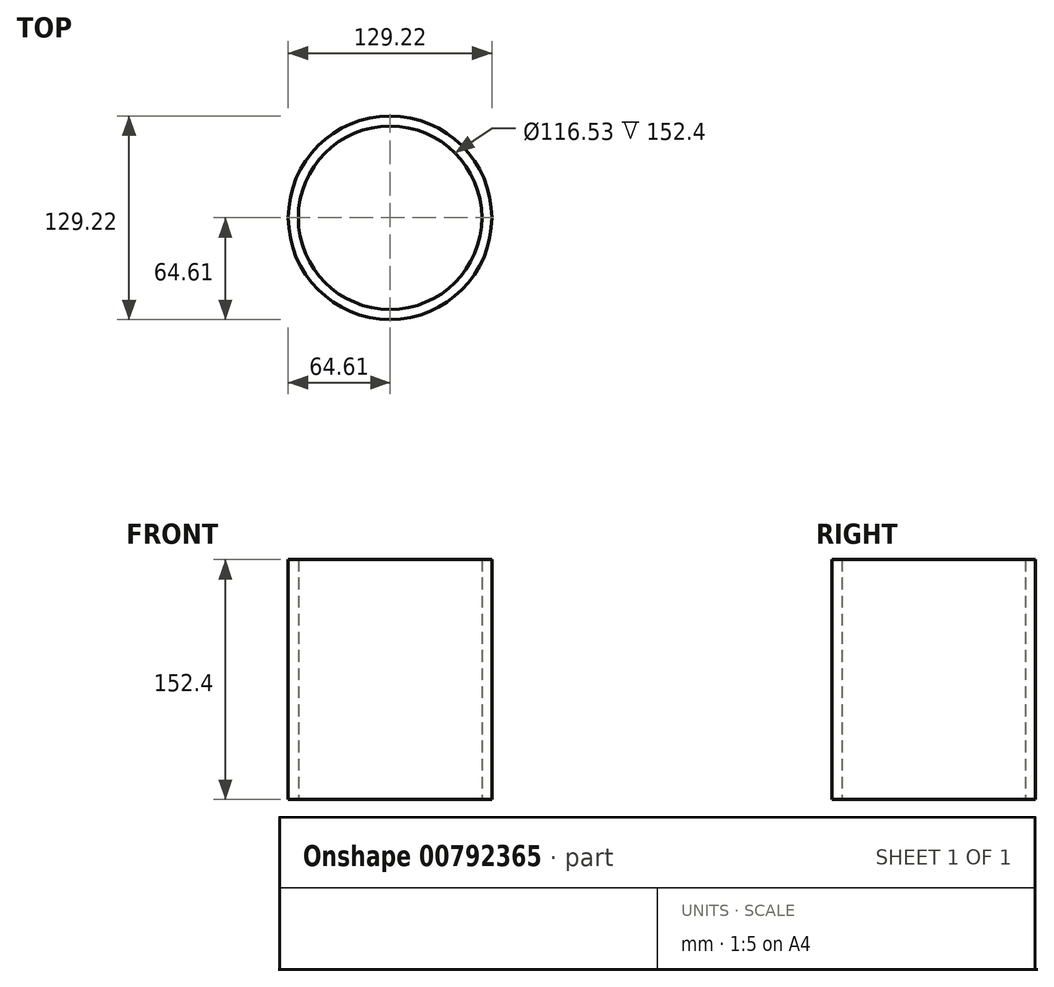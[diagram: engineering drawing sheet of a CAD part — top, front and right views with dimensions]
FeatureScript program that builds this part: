
annotation { "Feature Type Name" : "Feature", "Feature Type Description" : "" }
export const myFeature = defineFeature(function(context is Context, id is Id, definition is map)
    precondition{}
    {
        {
            var Q0;
            Q0=qCreatedBy(makeId("Top.planeOp"),FACE);
            var sketch = newSketch(context, id + "F0", { "sketchPlane" : qUnion([Q0])});
            skCircle(sketch, "E0", {"center": v(0, 0) * mm, "radius": 64.61 * mm});
            skCircle(sketch, "E1.0", {"center": v(0, 0) * mm, "radius": 58.26 * mm});
            skSolve(sketch);
        }
        {
            var Q0;
            Q0=makeQuery(id+"F0.imprint","IMPRINT",FACE,{"disambiguationData":[TD([[makeQuery(id+"F0.imprint","IMPRINT",EDGE,{"derivedFrom":sQuery(id+"F0.wireOp",EDGE,"E0")}),1.0]])]});
            extrude(context, id + "F1", {"entities" : qUnion([Q0]), "depth" : 76.2 * mm, "offsetDistance" : 25.4 * mm});
        }
        {
            var Q0;
            Q0=makeQuery(id+"F1.opExtrude","CAP_FACE",FACE,{"disambiguationData":[OSD([sQuery(id+"F0.wireOp",EDGE,"E0"),sQuery(id+"F0.wireOp",EDGE,"E1.0")])],"isStart":true});
            extrude(context, id + "F2", {"entities" : qUnion([Q0]), "operationType" : NewBodyOperationType.ADD, "depth" : 76.2 * mm, "offsetDistance" : 25.4 * mm});
        }
    });
